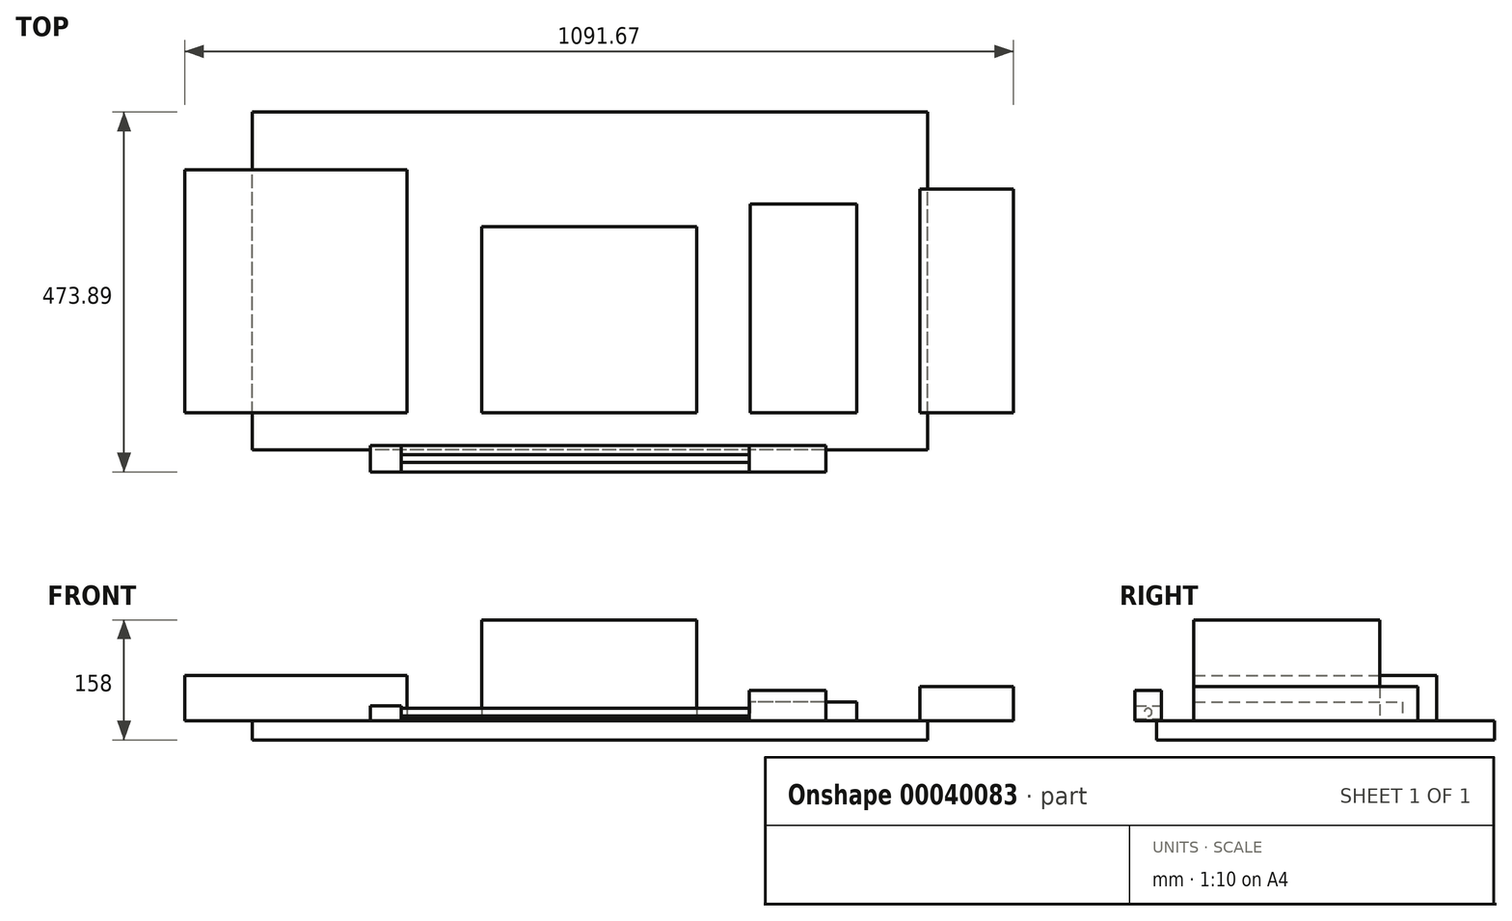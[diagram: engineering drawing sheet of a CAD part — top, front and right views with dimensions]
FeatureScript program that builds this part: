
annotation { "Feature Type Name" : "Feature", "Feature Type Description" : "" }
export const myFeature = defineFeature(function(context is Context, id is Id, definition is map)
    precondition{}
    {
        {
            var Q0;
            Q0=qCreatedBy(makeId("Top.planeOp"),FACE);
            var sketch = newSketch(context, id + "F0", { "sketchPlane" : qUnion([Q0])});
            skLineSegment(sketch, "E0.rect.bottom", {"start": v(70, -137.5) * mm, "end": v(-70, -137.5) * mm});
            skLineSegment(sketch, "E0.rect.top", {"start": v(70, 137.5) * mm, "end": v(-70, 137.5) * mm});
            skLineSegment(sketch, "E0.rect.left", {"start": v(70, -137.5) * mm, "end": v(70, 137.5) * mm});
            skLineSegment(sketch, "E0.rect.right", {"start": v(-70, -137.5) * mm, "end": v(-70, 137.5) * mm});
            skPoint(sketch, "E0.rect.middle", {"position": v(0, 0) * mm});
            skLineSegment(sketch, "E1.rect.bottom", {"start": v(276.42, -137.5) * mm, "end": v(153.42, -137.5) * mm});
            skLineSegment(sketch, "E1.rect.top", {"start": v(276.42, 157.5) * mm, "end": v(153.42, 157.5) * mm});
            skLineSegment(sketch, "E1.rect.left", {"start": v(276.42, -137.5) * mm, "end": v(276.42, 157.5) * mm});
            skLineSegment(sketch, "E1.rect.right", {"start": v(153.42, -137.5) * mm, "end": v(153.42, 157.5) * mm});
            skPoint(sketch, "E1.rect.middle", {"position": v(214.92, 10) * mm});
            skLineSegment(sketch, "E2.bottom", {"start": v(-140.98, -137.5) * mm, "end": v(-423.98, -137.5) * mm});
            skLineSegment(sketch, "E2.top", {"start": v(-140.98, 107.5) * mm, "end": v(-423.98, 107.5) * mm});
            skLineSegment(sketch, "E2.left", {"start": v(-140.98, -137.5) * mm, "end": v(-140.98, 107.5) * mm});
            skLineSegment(sketch, "E2.right", {"start": v(-423.98, -137.5) * mm, "end": v(-423.98, 107.5) * mm});
            skLineSegment(sketch, "E3.bottom", {"start": v(-522.25, -137.5) * mm, "end": v(-815.25, -137.5) * mm});
            skLineSegment(sketch, "E3.top", {"start": v(-522.25, 182.5) * mm, "end": v(-815.25, 182.5) * mm});
            skLineSegment(sketch, "E3.left", {"start": v(-522.25, -137.5) * mm, "end": v(-522.25, 182.5) * mm});
            skLineSegment(sketch, "E3.right", {"start": v(-815.25, -137.5) * mm, "end": v(-815.25, 182.5) * mm});
            skSolve(sketch);
        }
        {
            var Q0;
            Q0=makeQuery(id+"F0.imprint","IMPRINT",FACE,{"disambiguationData":[TD([[makeQuery(id+"F0.imprint","IMPRINT",EDGE,{"derivedFrom":sQuery(id+"F0.wireOp",EDGE,"E0.rect.bottom")}),-1.0]])]});
            extrude(context, id + "F1", {"entities" : qUnion([Q0]), "depth" : 25 * mm});
        }
        {
            var Q0;
            Q0=makeQuery(id+"F0.imprint","IMPRINT",FACE,{"disambiguationData":[TD([[makeQuery(id+"F0.imprint","IMPRINT",EDGE,{"derivedFrom":sQuery(id+"F0.wireOp",EDGE,"E1.rect.bottom")}),-1.0]])]});
            extrude(context, id + "F2", {"entities" : qUnion([Q0]), "depth" : 45 * mm});
        }
        {
            var Q0;
            Q0=makeQuery(id+"F0.imprint","IMPRINT",FACE,{"disambiguationData":[TD([[makeQuery(id+"F0.imprint","IMPRINT",EDGE,{"derivedFrom":sQuery(id+"F0.wireOp",EDGE,"E3.bottom")}),-1.0]])]});
            extrude(context, id + "F3", {"entities" : qUnion([Q0]), "depth" : 60 * mm});
        }
        {
            var Q0;
            Q0=makeQuery(id+"F0.imprint","IMPRINT",FACE,{"disambiguationData":[TD([[makeQuery(id+"F0.imprint","IMPRINT",EDGE,{"derivedFrom":sQuery(id+"F0.wireOp",EDGE,"E2.bottom")}),-1.0]])]});
            extrude(context, id + "F4", {"entities" : qUnion([Q0]), "depth" : 133 * mm});
        }
        {
            var Q0;
            Q0=makeQuery(id+"F4.opExtrude","CAP_FACE",FACE,{"disambiguationData":[OSD([sQuery(id+"F0.wireOp",EDGE,"E2.bottom"),sQuery(id+"F0.wireOp",EDGE,"E2.top"),sQuery(id+"F0.wireOp",EDGE,"E2.left"),sQuery(id+"F0.wireOp",EDGE,"E2.right")])],"isStart":true});
            var sketch = newSketch(context, id + "F5", { "sketchPlane" : qUnion([Q0])});
            skLineSegment(sketch, "E4.bottom", {"start": v(163.64, 186.38) * mm, "end": v(-726.36, 186.38) * mm});
            skLineSegment(sketch, "E4.top", {"start": v(163.64, -258.62) * mm, "end": v(-726.36, -258.62) * mm});
            skLineSegment(sketch, "E4.left", {"start": v(163.64, 186.38) * mm, "end": v(163.64, -258.62) * mm});
            skLineSegment(sketch, "E4.right", {"start": v(-726.36, 186.38) * mm, "end": v(-726.36, -258.62) * mm});
            skSolve(sketch);
        }
        {
            var Q0;
            Q0 = qSketchRegion(id + "F5", true);
            extrude(context, id + "F6", {"entities" : qUnion([Q0]), "depth" : 25 * mm});
        }
        {
            var Q0;
            Q0=qCreatedBy(makeId("Top.planeOp"),FACE);
            var sketch = newSketch(context, id + "F7", { "sketchPlane" : qUnion([Q0])});
            skLineSegment(sketch, "E5.bottom", {"start": v(-570.82, -215.27) * mm, "end": v(29.18, -215.27) * mm});
            skLineSegment(sketch, "E5.top", {"start": v(-570.82, -180.27) * mm, "end": v(29.18, -180.27) * mm});
            skLineSegment(sketch, "E5.left", {"start": v(-570.82, -215.27) * mm, "end": v(-570.82, -180.27) * mm});
            skLineSegment(sketch, "E5.right", {"start": v(29.18, -215.27) * mm, "end": v(29.18, -180.27) * mm});
            skLineSegment(sketch, "E6", {"start": v(-71.82, -180.27) * mm, "end": v(-71.82, -215.27) * mm});
            skLineSegment(sketch, "E7", {"start": v(-529.82, -180.27) * mm, "end": v(-529.82, -215.27) * mm});
            skSolve(sketch);
        }
        {
            var Q0;
            {var subQ1=sQuery(id+"F7.wireOp",EDGE,"E6");Q0=makeQuery(id+"F7.imprint","IMPRINT",FACE,{"disambiguationData":[TD([[makeQuery(id+"F7.imprint","IMPRINT",EDGE,{"derivedFrom":subQ1}),-1.0]])]});}
            var Q1;
            {var subQ1=sQuery(id+"F7.wireOp",EDGE,"E5.left");Q1=makeQuery(id+"F7.imprint","IMPRINT",FACE,{"disambiguationData":[TD([[makeQuery(id+"F7.imprint","IMPRINT",EDGE,{"derivedFrom":subQ1}),-1.0]])]});}
            var Q2;
            {var subQ1=sQuery(id+"F7.wireOp",EDGE,"E5.right");Q2=makeQuery(id+"F7.imprint","IMPRINT",FACE,{"disambiguationData":[TD([[makeQuery(id+"F7.imprint","IMPRINT",EDGE,{"derivedFrom":subQ1}),1.0]])]});}
            extrude(context, id + "F8", {"entities" : qUnion([Q0, Q1, Q2]), "depth" : 3 * mm});
        }
        {
            var Q0;
            {var subQ1=sQuery(id+"F7.wireOp",EDGE,"E5.left");Q0=makeQuery(id+"F7.imprint","IMPRINT",FACE,{"disambiguationData":[TD([[makeQuery(id+"F7.imprint","IMPRINT",EDGE,{"derivedFrom":subQ1}),-1.0]])]});}
            extrude(context, id + "F9", {"entities" : qUnion([Q0]), "operationType" : NewBodyOperationType.ADD, "depth" : 20 * mm});
        }
        {
            var Q0;
            {var subQ1=sQuery(id+"F7.wireOp",EDGE,"E5.right");Q0=makeQuery(id+"F7.imprint","IMPRINT",FACE,{"disambiguationData":[TD([[makeQuery(id+"F7.imprint","IMPRINT",EDGE,{"derivedFrom":subQ1}),1.0]])]});}
            extrude(context, id + "F10", {"entities" : qUnion([Q0]), "operationType" : NewBodyOperationType.ADD, "depth" : 40 * mm});
        }
        {
            var Q0;
            Q0=makeQuery(id+"F9.opExtrude","SWEPT_FACE",FACE,{"disambiguationData":[OSD([sQuery(id+"F7.wireOp",EDGE,"E7")])]});
            var sketch = newSketch(context, id + "F11", { "sketchPlane" : qUnion([Q0])});
            skCircle(sketch, "E8", {"center": v(-197.77, 11.5) * mm, "radius": 5 * mm});
            skPoint(sketch, "E8.centerSnap0", {"position": v(-215.27, 11.5) * mm});
            skPoint(sketch, "E8.centerSnap1", {"position": v(-197.77, 3) * mm});
            skSolve(sketch);
        }
        {
            var Q0;
            Q0=makeQuery(id+"F11.imprint","IMPRINT",FACE,{"disambiguationData":[TD([[makeQuery(id+"F11.imprint","IMPRINT",EDGE,{"derivedFrom":sQuery(id+"F11.wireOp",EDGE,"E8")}),1.0]])]});
            var Q1;
            Q1=makeQuery(id+"F10.opExtrude","SWEPT_FACE",FACE,{"disambiguationData":[OSD([sQuery(id+"F7.wireOp",EDGE,"E6")])]});
            extrude(context, id + "F12", {"entities" : qUnion([Q0]), "endBound" : BoundingType.UP_TO_SURFACE, "endBoundEntityFace" : qUnion([Q1]), "depth" : 25 * mm});
        }
    });
